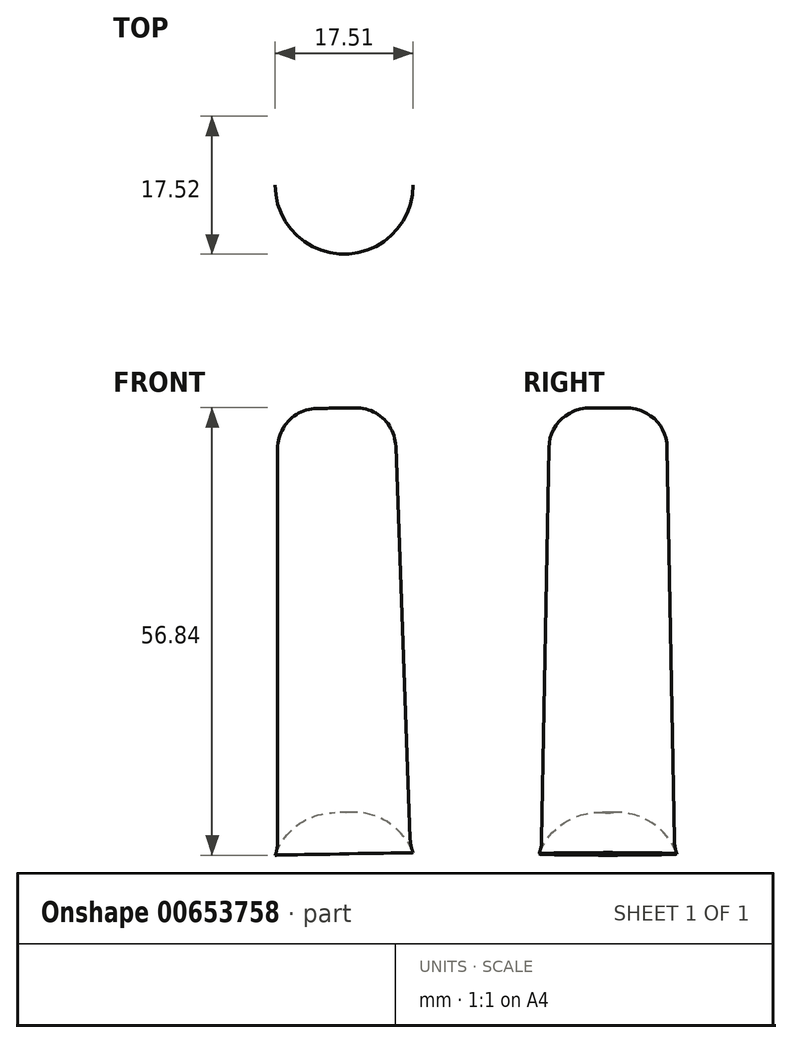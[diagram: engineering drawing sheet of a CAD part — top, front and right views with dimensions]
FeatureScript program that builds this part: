
annotation { "Feature Type Name" : "Feature", "Feature Type Description" : "" }
export const myFeature = defineFeature(function(context is Context, id is Id, definition is map)
    precondition{}
    {
        {
            var Q0;
            Q0=qCreatedBy(makeId("Front.planeOp"),FACE);
            var sketch = newSketch(context, id + "F0", { "sketchPlane" : qUnion([Q0])});
            skArc(sketch, "E0", {"start": v(-14.83, 0) * mm, "mid": v(-14, -8.42) * mm, "end": v(-6.17, -11.63) * mm});
            skLineSegment(sketch, "E1", {"start": v(-14.83, 0) * mm, "end": v(-14.83, 55.93) * mm});
            skLineSegment(sketch, "E2", {"start": v(-7.42, 56.06) * mm, "end": v(-14.83, 55.93) * mm});
            skLineSegment(sketch, "E3", {"start": v(-7.42, 56.06) * mm, "end": v(-6.17, -11.63) * mm});
            skPoint(sketch, "E4.orphan", {"position": v(0, 56.2) * mm});
            skSolve(sketch);
        }
        {
            var Q0;
            Q0=makeQuery(id+"F0.imprint","IMPRINT",FACE,{"disambiguationData":[TD([[makeQuery(id+"F0.imprint","IMPRINT",EDGE,{"derivedFrom":sQuery(id+"F0.wireOp",EDGE,"E0")}),1.0]])]});
            var Q1;
            Q1=sQuery(id+"F0.wireOp",EDGE,"E3");
            revolve(context, id + "F1", {"entities" : qUnion([Q0]), "axis" : qUnion([Q1]), "revolveType" : RevolveType.FULL});
        }
        {
            var Q0;
            Q0=makeQuery(id+"F1.opRevolve","SWEPT_FACE",FACE,{"disambiguationData":[OSD([sQuery(id+"F0.wireOp",EDGE,"E1")])]});
            fillet(context, id + "F2", {"entities" : qUnion([Q0]), "radius" : 5.08 * mm, "tangentPropagation" : true, "allowEdgeOverflow" : false});
        }
    });
